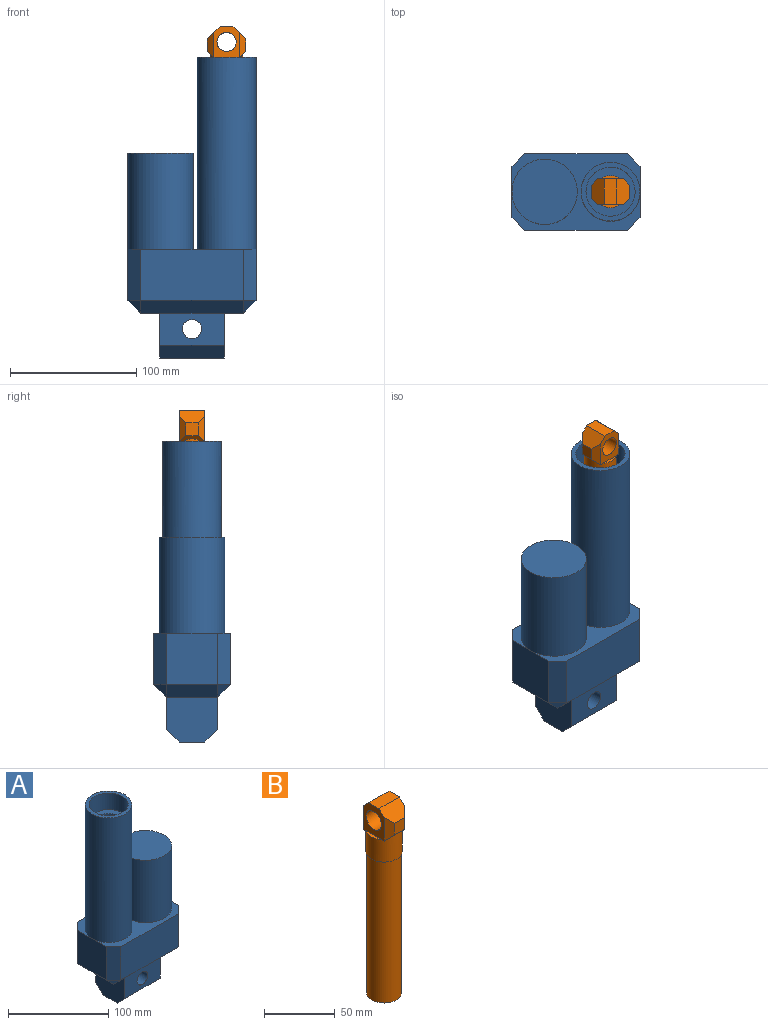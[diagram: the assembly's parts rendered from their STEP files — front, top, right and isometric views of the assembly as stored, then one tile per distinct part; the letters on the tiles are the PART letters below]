
ASSEMBLY  parts=2 mates=1
PART A: 35 faces, bbox 101.6x61x238.8 mm
  f0: plane 40.64x15.24mm, normal (0,0,-1), area 619.4mm2, adj f3,f16,f20,f21
  f1: plane 40.64x35.56mm, normal (-1,0,0), area 1341.9mm2, adj f2,f4,f5,f11,f24,f25
  f2: plane 50.8x25.4mm, normal (0,-1,0), area 1107.9mm2, adj f1,f3,f16,f25,f34
  f3: plane 40.64x35.56mm, normal (1,0,0), area 1341.9mm2, adj f0,f2,f4,f5,f24,f25
  f4: plane 50.8x25.4mm, normal (0,1,0), area 1107.9mm2, adj f1,f3,f20,f24,f34
  f5: plane 50.8x20.32mm, normal (0,0,-1), area 1032.3mm2, adj f1,f3,f24,f25
  f6: plane 81.28x40.64mm, normal (0,-1,0), area 3303.2mm2, adj f10,f12,f16,f17
  f7: plane 40.64x40.64mm, normal (1,0,0), area 1651.6mm2, adj f10,f17,f21,f23
  f8: plane 81.28x40.64mm, normal (0,1,0), area 3303.2mm2, adj f10,f14,f20,f23
  f9: plane 40.64x40.64mm, normal (-1,0,0), area 1651.6mm2, adj f10,f12,f14,f15
  f10: plane 101.6x60.96mm, normal (0,0,1), area 2162.9mm2, adj f6,f7,f8,f9,f12,f14,f17,f23
  f11: plane 40.64x15.24mm, normal (0,0,-1), area 619.4mm2, adj f1,f15,f16,f20
  f12: plane 40.64x10.16mm, normal (-0.71,-0.71,0), area 583.9mm2, adj f6,f9,f10,f13
  f13: plane 10.16x10.16mm, normal (-0.58,-0.58,-0.58), area 89.4mm2, adj f12,f15,f16
  f14: plane 40.64x10.16mm, normal (-0.71,0.71,0), area 583.9mm2, adj f8,f9,f10,f18
  f15: plane 40.64x10.16mm, normal (-0.71,0,-0.71), area 583.9mm2, adj f9,f11,f13,f18
  f16: plane 81.28x10.16mm, normal (0,-0.71,-0.71), area 1167.9mm2, adj f0,f2,f6,f11,f13,f19
  f17: plane 40.64x10.16mm, normal (0.71,-0.71,0), area 583.9mm2, adj f6,f7,f10,f19
  f18: plane 10.16x10.16mm, normal (-0.58,0.58,-0.58), area 89.4mm2, adj f14,f15,f20
  f19: plane 10.16x10.16mm, normal (0.58,-0.58,-0.58), area 89.4mm2, adj f16,f17,f21
  f20: plane 81.28x10.16mm, normal (0,0.71,-0.71), area 1167.9mm2, adj f0,f4,f8,f11,f18,f22
  f21: plane 40.64x10.16mm, normal (0.71,0,-0.71), area 583.9mm2, adj f0,f7,f19,f22
  f22: plane 10.16x10.16mm, normal (0.58,0.58,-0.58), area 89.4mm2, adj f20,f21,f23
  f23: plane 40.64x10.16mm, normal (0.71,0.71,0), area 583.9mm2, adj f7,f8,f10,f22
  f24: plane 50.8x10.16mm, normal (0,0.71,-0.71), area 729.9mm2, adj f1,f3,f4,f5
  f25: plane 50.8x10.16mm, normal (0,-0.71,-0.71), area 729.9mm2, adj f1,f2,f3,f5
  f26: cylinder r=23.37mm len=152.4mm, axis (0,0,-1), area 22376.2mm2, adj f10,f27
  f27: plane 46.74x46.74mm, normal (0,0,1), area 520.9mm2, adj f26,f32
  f28: cylinder r=25.91mm len=76.2mm, axis (0,0,-1), area 12404.2mm2, adj f10,f29
  f29: plane 51.82x51.82mm, normal (0,0,1), area 2108.7mm2, adj f28
  f30: cylinder r=12.7mm len=106.44mm, axis (0,0,1), area 8493.5mm2, adj f31,f33
  f31: plane 39x39mm, normal (0,0,1), area 687.9mm2, adj f30,f32
  f32: cylinder r=19.5mm len=39mm, axis (0,0,1), area 2450.4mm2, adj f27,f31
  f33: cone r=0mm half-angle=59deg, axis (0,0,1), area 591.1mm2, adj f30
  f34: cylinder r=7.62mm len=40.64mm, axis (0,1,0), area 1945.8mm2, adj f2,f4
PART B: 24 faces, bbox 25.4x30.5x166.6 mm
  f0: plane 2.54x2.54mm, normal (0,0,-1), area 2.9mm2, adj f5,f11,f22
  f1: plane 2.54x2.54mm, normal (0,0,-1), area 2.9mm2, adj f5,f13,f19
  f2: plane 15.24x2.54mm, normal (0,0,1), area 26.4mm2, adj f5,f13
  f3: cylinder r=12.19mm len=121.92mm, axis (0,0,-1), area 9339.6mm2, adj f4,f7
  f4: plane 24.38x24.38mm, normal (0,0,-1), area 467mm2, adj f3
  f5: cylinder r=12.7mm len=25.4mm, axis (0,0,-1), area 1595.4mm2, adj f0,f1,f2,f6,f7,f8,f9,f19
  f6: plane 15.24x2.54mm, normal (0,0,1), area 26.4mm2, adj f5,f11
  f7: plane 25.4x25.4mm, normal (0,0,-1), area 39.7mm2, adj f3,f5
  f8: plane 2.54x2.54mm, normal (0,0,-1), area 2.9mm2, adj f5,f11,f19
  f9: plane 2.54x2.54mm, normal (0,0,-1), area 2.9mm2, adj f5,f13,f22
  f10: plane 10.16x10.16mm, normal (0,-1,0), area 103.2mm2, adj f17,f21,f22,f23
  f11: plane 25.4x20.32mm, normal (1,0,0), area 307.9mm2, adj f0,f6,f8,f14,f15,f16,f17,f18
  f12: plane 10.16x10.16mm, normal (0,1,0), area 103.2mm2, adj f16,f18,f19,f20
  f13: plane 25.4x20.32mm, normal (-1,0,0), area 307.9mm2, adj f1,f2,f9,f14,f15,f16,f17,f20
  f14: plane 20.32x10.16mm, normal (0,0,1), area 206.5mm2, adj f11,f13,f16,f17
  f15: cylinder r=7.62mm len=20.32mm, axis (1,0,0), area 972.9mm2, adj f11,f13
  f16: plane 20.32x10.16mm, normal (0,0.71,0.71), area 255.5mm2, adj f11,f12,f13,f14,f18,f20
  f17: plane 20.32x10.16mm, normal (0,-0.71,0.71), area 255.5mm2, adj f10,f11,f13,f14,f21,f23
  f18: plane 20.32x5.08mm, normal (0.71,0.71,0), area 109.5mm2, adj f11,f12,f16,f19
  f19: plane 20.32x5.08mm, normal (0,0.71,-0.71), area 72.2mm2, adj f1,f5,f8,f12,f18,f20
  f20: plane 20.32x5.08mm, normal (-0.71,0.71,0), area 109.5mm2, adj f12,f13,f16,f19
  f21: plane 20.32x5.08mm, normal (0.71,-0.71,0), area 109.5mm2, adj f10,f11,f17,f22
  f22: plane 20.32x5.08mm, normal (0,-0.71,-0.71), area 72.2mm2, adj f0,f5,f9,f10,f21,f23
  f23: plane 20.32x5.08mm, normal (-0.71,-0.71,0), area 109.5mm2, adj f10,f13,f17,f22
PLACE A rot(axis=(0,0,-1),180deg) t=(-349.45,-164.77,-6.34)mm fixed
PLACE B rot(axis=(0,0,-1),90deg) t=(54.03,-163.63,90.5)mm
MATE slider B.f3 <-> A.f26  axis (0,0,-1) through (-121.96,-91.94,90.5)mm
